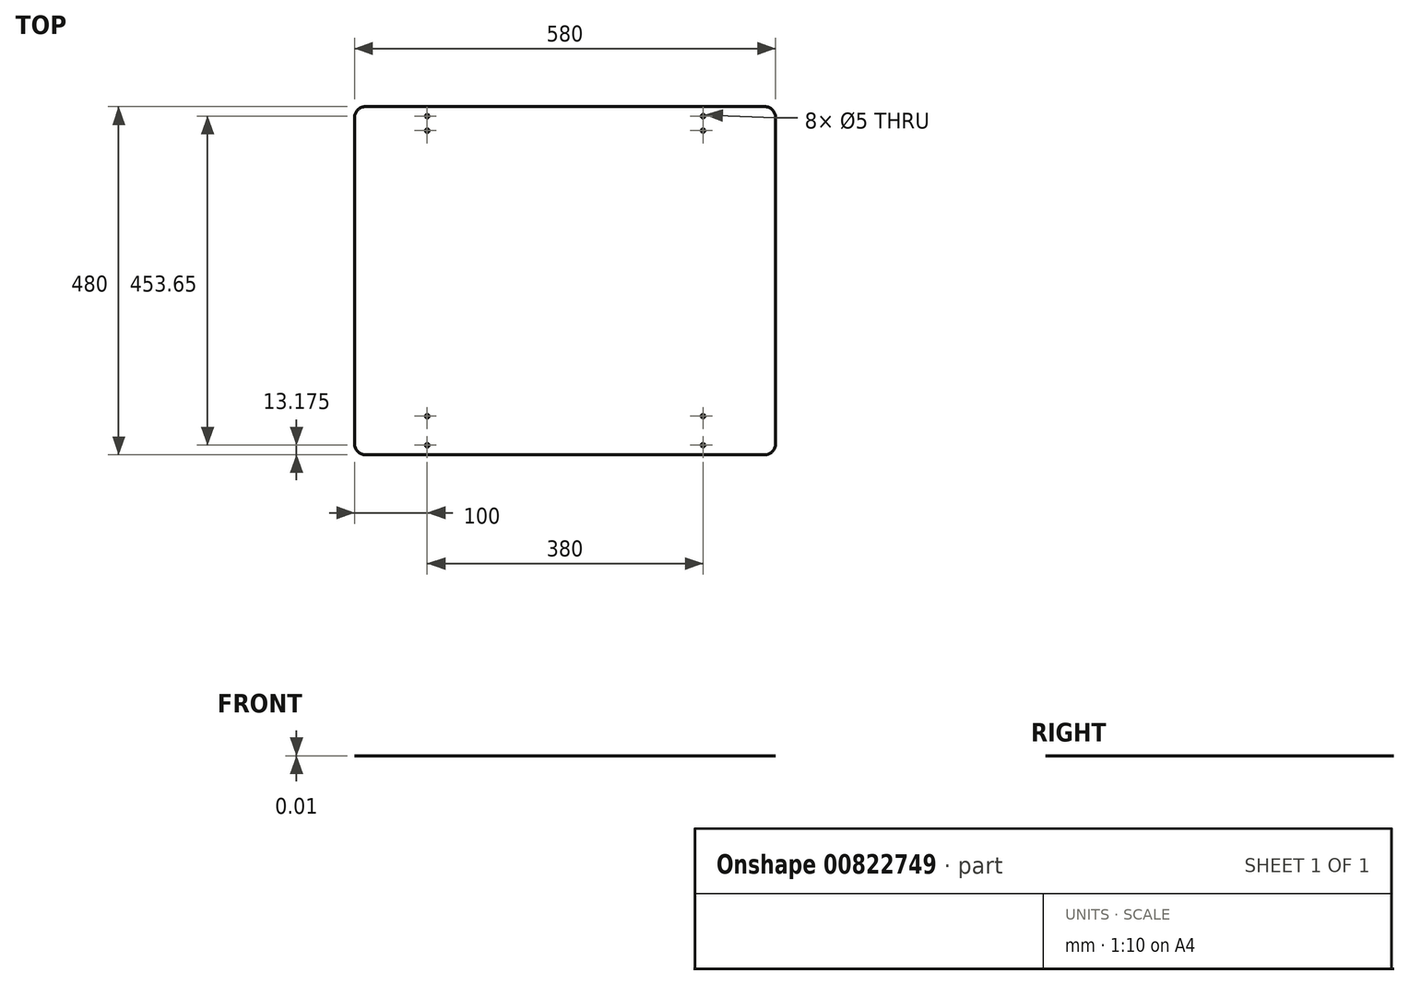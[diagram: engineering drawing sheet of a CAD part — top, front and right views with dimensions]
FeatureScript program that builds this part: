
annotation { "Feature Type Name" : "Feature", "Feature Type Description" : "" }
export const myFeature = defineFeature(function(context is Context, id is Id, definition is map)
    precondition{}
    {
        {
            var Q0;
            Q0=qCreatedBy(makeId("Top.planeOp"),FACE);
            var sketch = newSketch(context, id + "F0", { "sketchPlane" : qUnion([Q0])});
            skCircle(sketch, "E0.9", {"center": v(190, 206.82) * mm, "radius": 2.5 * mm});
            skCircle(sketch, "E0.10", {"center": v(190, 226.82) * mm, "radius": 2.5 * mm});
            skPoint(sketch, "E1.0", {"position": v(0, 0) * mm});
            skLineSegment(sketch, "E2", {"start": v(-25, 0) * mm, "end": v(25, 0) * mm, "construction": true});
            skLineSegment(sketch, "E3.bottom", {"start": v(275, -240) * mm, "end": v(-275, -240) * mm});
            skLineSegment(sketch, "E3.top", {"start": v(275, 240) * mm, "end": v(-275, 240) * mm});
            skLineSegment(sketch, "E3.left", {"start": v(290, -225) * mm, "end": v(290, 225) * mm});
            skLineSegment(sketch, "E3.right", {"start": v(-290, -225) * mm, "end": v(-290, 225) * mm});
            skPoint(sketch, "E4.visualSharp", {"position": v(-290, 240) * mm});
            skArc(sketch, "E4.filletArc", {"start": v(-275, 240) * mm, "mid": v(-285.6, 235.6) * mm, "end": v(-290, 225) * mm});
            skPoint(sketch, "E5.visualSharp", {"position": v(290, 240) * mm});
            skArc(sketch, "E5.filletArc", {"start": v(290, 225) * mm, "mid": v(285.6, 235.6) * mm, "end": v(275, 240) * mm});
            skPoint(sketch, "E6.visualSharp", {"position": v(290, -240) * mm});
            skArc(sketch, "E6.filletArc", {"start": v(275, -240) * mm, "mid": v(285.6, -235.6) * mm, "end": v(290, -225) * mm});
            skPoint(sketch, "E7.visualSharp", {"position": v(-290, -240) * mm});
            skArc(sketch, "E7.filletArc", {"start": v(-290, -225) * mm, "mid": v(-285.6, -235.6) * mm, "end": v(-275, -240) * mm});
            skCircle(sketch, "E8.MirrorC", {"center": v(190, -226.82) * mm, "radius": 2.5 * mm});
            skCircle(sketch, "E9.MirrorC", {"center": v(190, -186.82) * mm, "radius": 2.5 * mm});
            skLineSegment(sketch, "E10", {"start": v(0, 25) * mm, "end": v(0, -25) * mm, "construction": true});
            skCircle(sketch, "E11.MirrorC", {"center": v(-190, -226.82) * mm, "radius": 2.5 * mm});
            skCircle(sketch, "E12.MirrorC", {"center": v(-190, -186.82) * mm, "radius": 2.5 * mm});
            skLineSegment(sketch, "E13", {"start": v(190, 226.82) * mm, "end": v(190, 206.82) * mm});
            skCircle(sketch, "E14.MirrorC", {"center": v(-190, 226.83) * mm, "radius": 2.5 * mm});
            skCircle(sketch, "E15.MirrorC", {"center": v(-190, 206.83) * mm, "radius": 2.5 * mm});
            skLineSegment(sketch, "E16", {"start": v(190, -186.82) * mm, "end": v(190, -226.82) * mm, "construction": true});
            skSolve(sketch);
        }
        {
            var Q0;
            Q0=qSketchRegion(id+"F0",true);
            extrude(context, id + "F1", {"entities" : qUnion([Q0]), "oppositeDirection" : true, "depth" : 1 / 101.6 * mm, "offsetDistance" : 25 * mm});
        }
    });
